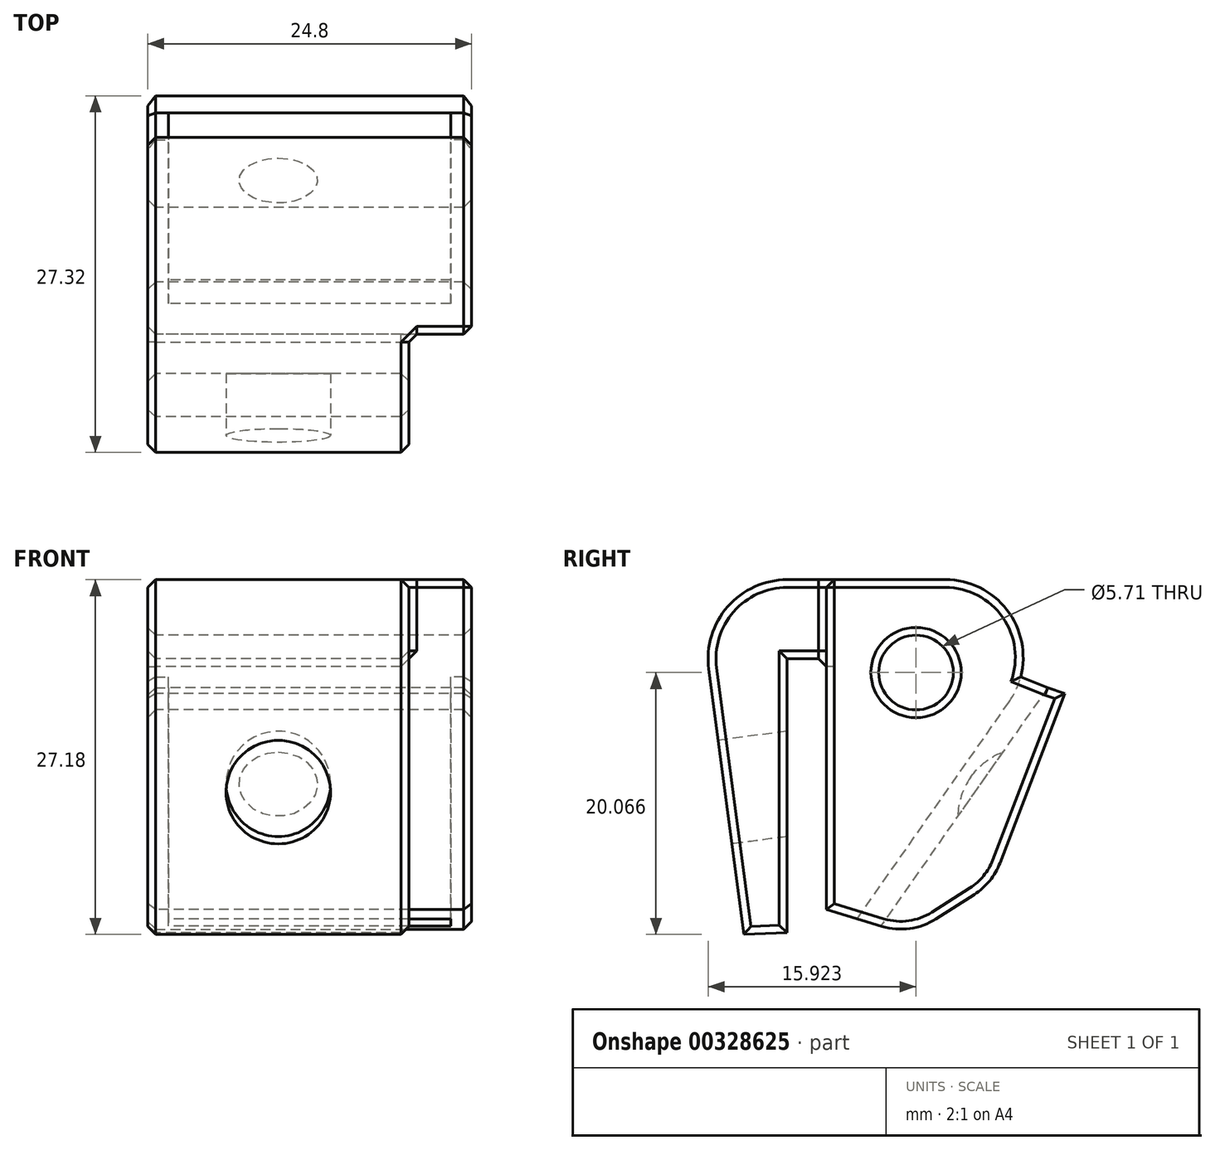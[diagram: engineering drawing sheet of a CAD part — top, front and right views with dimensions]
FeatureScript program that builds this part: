
annotation { "Feature Type Name" : "Feature", "Feature Type Description" : "" }
export const myFeature = defineFeature(function(context is Context, id is Id, definition is map)
    precondition{}
    {
        {
            var Q0;
            Q0=qCreatedBy(makeId("Right.planeOp"),FACE);
            var sketch = newSketch(context, id + "F0", { "sketchPlane" : qUnion([Q0])});
            skLineSegment(sketch, "E0", {"start": v(23.41, 24.6) * mm, "end": v(26.71, 24.72) * mm});
            skLineSegment(sketch, "E1", {"start": v(26.71, 24.72) * mm, "end": v(26.71, 45.72) * mm});
            skLineSegment(sketch, "E2", {"start": v(26.71, 45.72) * mm, "end": v(29.71, 45.72) * mm});
            skLineSegment(sketch, "E3", {"start": v(29.71, 45.72) * mm, "end": v(29.71, 26.5) * mm});
            skLineSegment(sketch, "E4", {"start": v(29.71, 26.5) * mm, "end": v(40.4, 23.27) * mm});
            skLineSegment(sketch, "E5", {"start": v(40.4, 23.27) * mm, "end": v(47.98, 43.03) * mm});
            skLineSegment(sketch, "E6", {"start": v(47.98, 43.03) * mm, "end": v(46.66, 43.48) * mm});
            skLineSegment(sketch, "E7", {"start": v(46.66, 43.48) * mm, "end": v(35.19, 27.1) * mm});
            skLineSegment(sketch, "E8", {"start": v(35.19, 27.1) * mm, "end": v(33.71, 28.13) * mm});
            skLineSegment(sketch, "E9", {"start": v(33.71, 28.13) * mm, "end": v(50.27, 51.77) * mm});
            skLineSegment(sketch, "E10", {"start": v(50.27, 51.77) * mm, "end": v(19.8, 51.77) * mm});
            skLineSegment(sketch, "E11", {"start": v(19.8, 51.77) * mm, "end": v(23.41, 24.6) * mm});
            skCircle(sketch, "E12", {"center": v(36.58, 44.66) * mm, "radius": 2.86 * mm});
            skArc(sketch, "E13", {"start": v(43.7, 42.4) * mm, "mid": v(44.11, 48.57) * mm, "end": v(38.83, 51.77) * mm});
            skArc(sketch, "E14", {"start": v(26.71, 51.77) * mm, "mid": v(22.16, 49.7) * mm, "end": v(20.71, 44.92) * mm});
            skLineSegment(sketch, "E15", {"start": v(42.42, 28.54) * mm, "end": v(36.17, 24.55) * mm});
            skSolve(sketch);
        }
        {
            var Q0;
            {var subQ8=sQuery(id+"F0.wireOp",EDGE,"E0");Q0=makeQuery(id+"F0.imprint","IMPRINT",FACE,{"disambiguationData":[TD([[makeQuery(id+"F0.imprint","IMPRINT",EDGE,{"derivedFrom":subQ8}),1.0]])]});}
            extrude(context, id + "F1", {"entities" : qUnion([Q0]), "endBound" : BoundingType.SYMMETRIC, "depth" : 20 * mm});
        }
        {
            var Q0;
            Q0=makeQuery(id+"F1.opExtrude","SWEPT_FACE",FACE,{"disambiguationData":[OSD([sQuery(id+"F0.wireOp",EDGE,"E11")])]});
            var sketch = newSketch(context, id + "F2", { "sketchPlane" : qUnion([Q0])});
            skLineSegment(sketch, "E16", {"start": v(0, 21.3) * mm, "end": v(0, 32.3) * mm, "construction": true});
            skCircle(sketch, "E17", {"center": v(0, 32.3) * mm, "radius": 4 * mm});
            skSolve(sketch);
        }
        {
            var Q0;
            Q0 = qSketchRegion(id + "F2", true);
            var Q1;
            Q1=makeQuery(id+"F1.opExtrude","SWEPT_FACE",FACE,{"disambiguationData":[OSD([sQuery(id+"F0.wireOp",EDGE,"E1")])]});
            extrude(context, id + "F3", {"entities" : qUnion([Q0]), "operationType" : NewBodyOperationType.REMOVE, "endBound" : BoundingType.UP_TO_SURFACE, "oppositeDirection" : true, "endBoundEntityFace" : qUnion([Q1]), "depth" : 25 * mm});
        }
        {
            var Q0;
            Q0=makeQuery(id+"F1.opExtrude","SWEPT_FACE",FACE,{"disambiguationData":[OSD([sQuery(id+"F0.wireOp",EDGE,"E7")])]});
            var sketch = newSketch(context, id + "F4", { "sketchPlane" : qUnion([Q0])});
            skLineSegment(sketch, "E18.0", {"start": v(10, 42.38) * mm, "end": v(-10, 42.38) * mm});
            skLineSegment(sketch, "E19", {"start": v(0, 42.38) * mm, "end": v(0, 53.38) * mm});
            skPoint(sketch, "E19.endSnap0", {"position": v(0, 42.38) * mm});
            skSolve(sketch);
        }
        {
            var Q0;
            Q0=sQuery(id+"F4.wireOp",EDGE,"E19");
            extrude(context, id + "F5", {"bodyType" : ToolBodyType.SURFACE, "surfaceEntities" : qUnion([Q0]), "depth" : 5 * mm});
        }
        {
            var Q0;
            Q0=makeQuery(id+"F5.opExtrude","SWEPT_FACE",FACE,{"disambiguationData":[OSD([sQuery(id+"F4.wireOp",EDGE,"E19")])]});
            var sketch = newSketch(context, id + "F6", { "sketchPlane" : qUnion([Q0])});
            skLineSegment(sketch, "E20", {"start": v(39.77, 33.65) * mm, "end": v(39.04, 34.17) * mm});
            skLineSegment(sketch, "E21", {"start": v(39.04, 34.17) * mm, "end": v(40.76, 36.63) * mm});
            skArc(sketch, "E22", {"start": v(40.76, 36.63) * mm, "mid": v(40.05, 35.21) * mm, "end": v(39.77, 33.65) * mm});
            skSolve(sketch);
        }
        {
            var Q0;
            {var subQ0=sQuery(id+"F6.wireOp",EDGE,"E22");Q0=makeQuery(id+"F6.imprint","IMPRINT",FACE,{"disambiguationData":[TD([[makeQuery(id+"F6.imprint","IMPRINT",EDGE,{"derivedFrom":subQ0}),1.0]])]});}
            var Q1;
            Q1=makeQuery(id+"F5.opExtrude","SWEPT_EDGE",EDGE,{"disambiguationData":[OSD([sQuery(id+"F4.wireOp",VERTEX,"E19.end")])]});
            revolve(context, id + "F7", {"operationType" : NewBodyOperationType.ADD, "entities" : qUnion([Q0]), "axis" : qUnion([Q1]), "revolveType" : RevolveType.FULL});
        }
        {
            var Q0;
            Q0=makeQuery(id+"F1.opExtrude","CAP_FACE",FACE,{"disambiguationData":[OSD([sQuery(id+"F0.wireOp",EDGE,"E0"),sQuery(id+"F0.wireOp",EDGE,"E1"),sQuery(id+"F0.wireOp",EDGE,"E2"),sQuery(id+"F0.wireOp",EDGE,"E3"),sQuery(id+"F0.wireOp",EDGE,"E4"),sQuery(id+"F0.wireOp",EDGE,"E5"),sQuery(id+"F0.wireOp",EDGE,"E6"),sQuery(id+"F0.wireOp",EDGE,"E7"),sQuery(id+"F0.wireOp",EDGE,"E8"),sQuery(id+"F0.wireOp",EDGE,"E9"),sQuery(id+"F0.wireOp",EDGE,"E10"),sQuery(id+"F0.wireOp",EDGE,"E11"),sQuery(id+"F0.wireOp",EDGE,"E12"),sQuery(id+"F0.wireOp",EDGE,"E13"),sQuery(id+"F0.wireOp",EDGE,"E14"),sQuery(id+"F0.wireOp",EDGE,"E15")])],"isStart":false});
            var sketch = newSketch(context, id + "F8", { "sketchPlane" : qUnion([Q0])});
            skLineSegment(sketch, "E23.0.0", {"start": v(38.83, 51.77) * mm, "end": v(26.71, 51.77) * mm});
            skArc(sketch, "E23.0.1", {"start": v(26.71, 51.77) * mm, "mid": v(22.16, 49.7) * mm, "end": v(20.71, 44.92) * mm});
            skLineSegment(sketch, "E23.0.2", {"start": v(20.71, 44.92) * mm, "end": v(23.41, 24.6) * mm});
            skLineSegment(sketch, "E23.0.3", {"start": v(23.41, 24.6) * mm, "end": v(26.71, 24.72) * mm});
            skLineSegment(sketch, "E23.0.4", {"start": v(26.71, 24.72) * mm, "end": v(26.71, 45.72) * mm});
            skLineSegment(sketch, "E23.0.5", {"start": v(26.71, 45.72) * mm, "end": v(29.71, 45.72) * mm});
            skLineSegment(sketch, "E23.0.6", {"start": v(29.71, 45.72) * mm, "end": v(29.71, 26.5) * mm});
            skLineSegment(sketch, "E23.0.7", {"start": v(29.71, 26.5) * mm, "end": v(36.17, 24.55) * mm});
            skLineSegment(sketch, "E23.0.8", {"start": v(36.17, 24.55) * mm, "end": v(42.42, 28.54) * mm});
            skLineSegment(sketch, "E23.0.9", {"start": v(42.42, 28.54) * mm, "end": v(47.98, 43.03) * mm});
            skLineSegment(sketch, "E23.0.10", {"start": v(47.98, 43.03) * mm, "end": v(46.66, 43.48) * mm});
            skLineSegment(sketch, "E23.0.11", {"start": v(46.66, 43.48) * mm, "end": v(35.19, 27.1) * mm});
            skLineSegment(sketch, "E23.0.12", {"start": v(35.19, 27.1) * mm, "end": v(33.71, 28.13) * mm});
            skLineSegment(sketch, "E23.0.13", {"start": v(33.71, 28.13) * mm, "end": v(43.7, 42.4) * mm});
            skArc(sketch, "E23.0.14", {"start": v(43.7, 42.4) * mm, "mid": v(44.11, 48.57) * mm, "end": v(38.83, 51.77) * mm});
            skLineSegment(sketch, "E24", {"start": v(29.71, 45.72) * mm, "end": v(29.71, 51.77) * mm});
            skLineSegment(sketch, "E25", {"start": v(46.66, 43.48) * mm, "end": v(44.6, 44.32) * mm});
            skSolve(sketch);
        }
        {
            var Q0;
            Q0=makeQuery(id+"F8.imprint","IMPRINT",FACE,{"disambiguationData":[TD([[makeQuery(id+"F8.imprint","IMPRINT",EDGE,{"derivedFrom":sQuery(id+"F8.wireOp",EDGE,"E23.0.6")}),1.0]])]});
            extrude(context, id + "F9", {"entities" : qUnion([Q0]), "operationType" : NewBodyOperationType.ADD, "depth" : 3.2 * mm});
        }
        {
            var Q0;
            Q0=makeQuery(id+"F8.imprint","IMPRINT",FACE,{"disambiguationData":[TD([[makeQuery(id+"F8.imprint","IMPRINT",EDGE,{"derivedFrom":sQuery(id+"F8.wireOp",EDGE,"E23.0.6")}),1.0]])]});
            var Q1;
            Q1=makeQuery(id+"F8.imprint","IMPRINT",FACE,{"disambiguationData":[TD([[makeQuery(id+"F8.imprint","IMPRINT",EDGE,{"derivedFrom":sQuery(id+"F8.wireOp",EDGE,"E23.0.11")}),-1.0]])]});
            extrude(context, id + "F10", {"entities" : qUnion([Q0, Q1]), "operationType" : NewBodyOperationType.ADD, "depth" : 4.8 * mm, "hasSecondDirection" : true, "secondDirectionOppositeDirection" : false, "secondDirectionDepth" : 3.2 * mm});
        }
        {
            var Q0;
            Q0=makeQuery(id+"F8.imprint","IMPRINT",FACE,{"disambiguationData":[TD([[makeQuery(id+"F8.imprint","IMPRINT",EDGE,{"derivedFrom":sQuery(id+"F8.wireOp",EDGE,"E23.0.6")}),1.0]])]});
            var Q1;
            Q1=makeQuery(id+"F8.imprint","IMPRINT",FACE,{"disambiguationData":[TD([[makeQuery(id+"F8.imprint","IMPRINT",EDGE,{"derivedFrom":sQuery(id+"F8.wireOp",EDGE,"E23.0.11")}),-1.0]])]});
            extrude(context, id + "F11", {"entities" : qUnion([Q0, Q1]), "operationType" : NewBodyOperationType.ADD, "oppositeDirection" : true, "depth" : 20 * mm, "hasSecondDirection" : true, "secondDirectionOppositeDirection" : true, "secondDirectionDepth" : (20 - 1.6) * mm});
        }
        {
            var Q0;
            Q0=makeQuery(id+"F9.boolean.opBoolean","MERGE",FACE,{"derivedFrom":[makeQuery(id+"F1.opExtrude","SWEPT_FACE",FACE,{"disambiguationData":[OSD([sQuery(id+"F0.wireOp",EDGE,"E8")])]}),makeQuery(id+"F9.opExtrude","SWEPT_FACE",FACE,{"disambiguationData":[OSD([sQuery(id+"F8.wireOp",EDGE,"E23.0.12")])]})]});
            extrude(context, id + "F12", {"entities" : qUnion([Q0]), "operationType" : NewBodyOperationType.REMOVE, "oppositeDirection" : true, "depth" : 25 * mm});
        }
        {
            var Q0;
            {var subQ0=sQuery(id+"F8.wireOp",EDGE,"E23.0.8");var subQ1=sQuery(id+"F8.wireOp",EDGE,"E23.0.7");Q0=makeQuery(id+"F10.boolean.opBoolean","MERGE",EDGE,{"derivedFrom":[makeQuery(id+"F9.boolean.opBoolean","MERGE",EDGE,{"derivedFrom":[makeQuery(id+"F1.opExtrude","SWEPT_EDGE",EDGE,{"disambiguationData":[OSD([sQuery(id+"F0.wireOp",EDGE,"E4"),sQuery(id+"F0.wireOp",EDGE,"E15")])]}),makeQuery(id+"F9.opExtrude","SWEPT_EDGE",EDGE,{"disambiguationData":[OSD([subQ1,subQ0])]})]}),makeQuery(id+"F10.opExtrude","SWEPT_EDGE",EDGE,{"disambiguationData":[OSD([subQ1,subQ0])]})]});}
            var Q1;
            {var subQ0=sQuery(id+"F8.wireOp",EDGE,"E23.0.9");var subQ1=sQuery(id+"F8.wireOp",EDGE,"E23.0.8");Q1=makeQuery(id+"F10.boolean.opBoolean","MERGE",EDGE,{"derivedFrom":[makeQuery(id+"F9.boolean.opBoolean","MERGE",EDGE,{"derivedFrom":[makeQuery(id+"F1.opExtrude","SWEPT_EDGE",EDGE,{"disambiguationData":[OSD([sQuery(id+"F0.wireOp",EDGE,"E5"),sQuery(id+"F0.wireOp",EDGE,"E15")])]}),makeQuery(id+"F9.opExtrude","SWEPT_EDGE",EDGE,{"disambiguationData":[OSD([subQ1,subQ0])]})]}),makeQuery(id+"F10.opExtrude","SWEPT_EDGE",EDGE,{"disambiguationData":[OSD([subQ1,subQ0])]})]});}
            fillet(context, id + "F13", {"entities" : qUnion([Q0, Q1]), "radius" : 5 * mm, "tangentPropagation" : true, "allowEdgeOverflow" : false});
        }
        {
            var Q0;
            Q0=makeQuery(id+"F10.opExtrude","CAP_FACE",FACE,{"disambiguationData":[OSD([sQuery(id+"F0.wireOp",EDGE,"E12"),sQuery(id+"F8.wireOp",EDGE,"E23.0.0"),sQuery(id+"F8.wireOp",EDGE,"E23.0.6"),sQuery(id+"F8.wireOp",EDGE,"E23.0.7"),sQuery(id+"F8.wireOp",EDGE,"E23.0.8"),sQuery(id+"F8.wireOp",EDGE,"E23.0.9"),sQuery(id+"F8.wireOp",EDGE,"E23.0.10"),sQuery(id+"F8.wireOp",EDGE,"E23.0.13"),sQuery(id+"F8.wireOp",EDGE,"E23.0.14"),sQuery(id+"F8.wireOp",EDGE,"E24"),sQuery(id+"F8.wireOp",EDGE,"Rzi3c9Y5-5g1T-1iqe-qzWU-DZqvRk0hnTb4")])],"isStart":false});
            var Q1;
            {var subQ0=sQuery(id+"F0.wireOp",EDGE,"E12");Q1=makeQuery(id+"F11.boolean.opBoolean","MERGE",FACE,{"derivedFrom":[makeQuery(id+"F1.opExtrude","CAP_FACE",FACE,{"disambiguationData":[OSD([sQuery(id+"F0.wireOp",EDGE,"E0"),sQuery(id+"F0.wireOp",EDGE,"E1"),sQuery(id+"F0.wireOp",EDGE,"E2"),sQuery(id+"F0.wireOp",EDGE,"E3"),sQuery(id+"F0.wireOp",EDGE,"E4"),sQuery(id+"F0.wireOp",EDGE,"E5"),sQuery(id+"F0.wireOp",EDGE,"E6"),sQuery(id+"F0.wireOp",EDGE,"E7"),sQuery(id+"F0.wireOp",EDGE,"E8"),sQuery(id+"F0.wireOp",EDGE,"E9"),sQuery(id+"F0.wireOp",EDGE,"E10"),sQuery(id+"F0.wireOp",EDGE,"E11"),subQ0,sQuery(id+"F0.wireOp",EDGE,"E13"),sQuery(id+"F0.wireOp",EDGE,"E14"),sQuery(id+"F0.wireOp",EDGE,"E15")])],"isStart":true}),makeQuery(id+"F11.opExtrude","CAP_FACE",FACE,{"disambiguationData":[OSD([subQ0,sQuery(id+"F8.wireOp",EDGE,"E23.0.0"),sQuery(id+"F8.wireOp",EDGE,"E23.0.6"),sQuery(id+"F8.wireOp",EDGE,"E23.0.7"),sQuery(id+"F8.wireOp",EDGE,"E23.0.8"),sQuery(id+"F8.wireOp",EDGE,"E23.0.9"),sQuery(id+"F8.wireOp",EDGE,"E23.0.10"),sQuery(id+"F8.wireOp",EDGE,"E23.0.13"),sQuery(id+"F8.wireOp",EDGE,"E23.0.14"),sQuery(id+"F8.wireOp",EDGE,"E24"),sQuery(id+"F8.wireOp",EDGE,"Rzi3c9Y5-5g1T-1iqe-qzWU-DZqvRk0hnTb4")])],"isStart":false})]});}
            var Q2;
            Q2=makeQuery(id+"F1.opExtrude","CAP_FACE",FACE,{"disambiguationData":[OSD([sQuery(id+"F0.wireOp",EDGE,"E0"),sQuery(id+"F0.wireOp",EDGE,"E1"),sQuery(id+"F0.wireOp",EDGE,"E2"),sQuery(id+"F0.wireOp",EDGE,"E3"),sQuery(id+"F0.wireOp",EDGE,"E4"),sQuery(id+"F0.wireOp",EDGE,"E5"),sQuery(id+"F0.wireOp",EDGE,"E6"),sQuery(id+"F0.wireOp",EDGE,"E7"),sQuery(id+"F0.wireOp",EDGE,"E8"),sQuery(id+"F0.wireOp",EDGE,"E9"),sQuery(id+"F0.wireOp",EDGE,"E10"),sQuery(id+"F0.wireOp",EDGE,"E11"),sQuery(id+"F0.wireOp",EDGE,"E12"),sQuery(id+"F0.wireOp",EDGE,"E13"),sQuery(id+"F0.wireOp",EDGE,"E14"),sQuery(id+"F0.wireOp",EDGE,"E15")])],"isStart":false});
            chamfer(context, id + "F14", {"entities" : qUnion([Q0, Q1, Q2]), "width" : 0.6 * mm, "tangentPropagation" : true});
        }
    });
